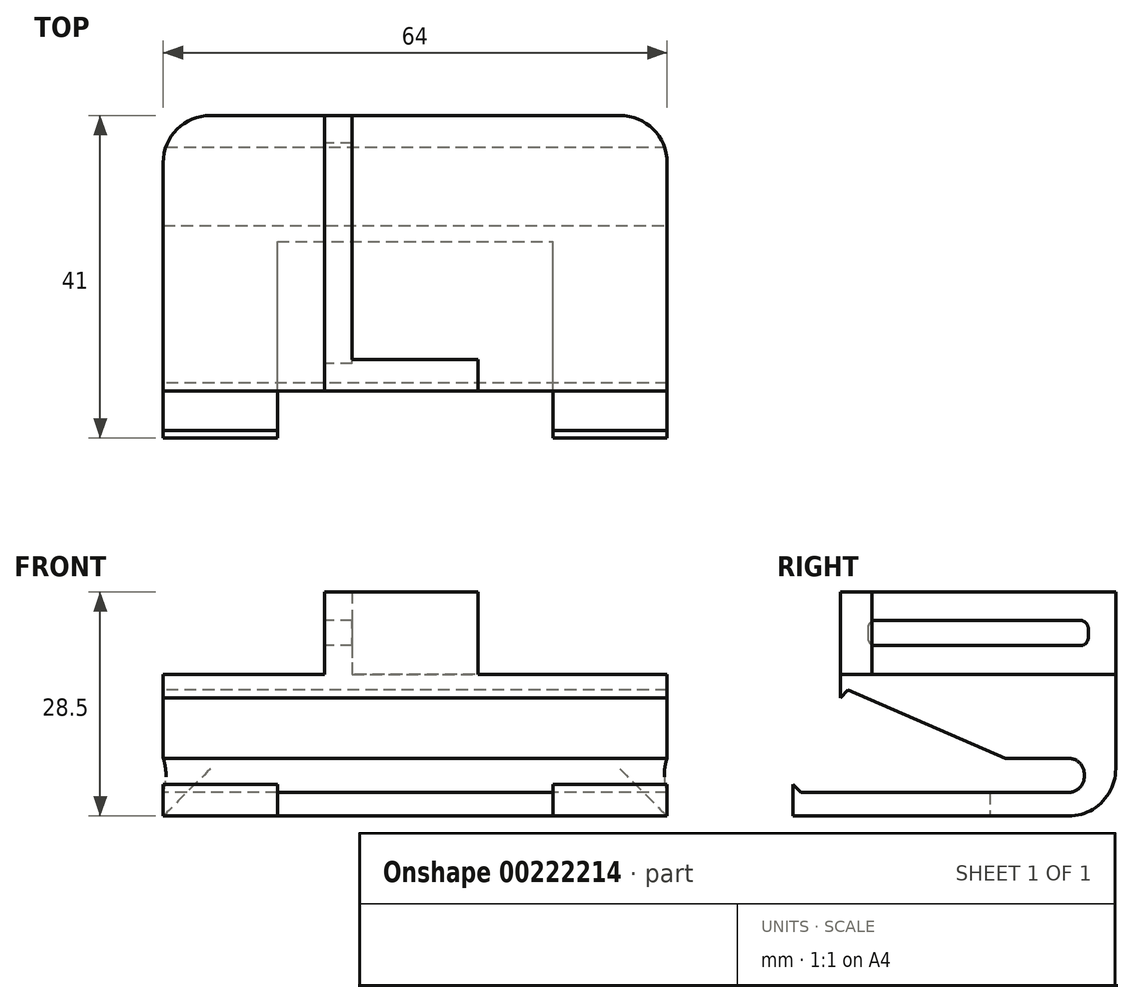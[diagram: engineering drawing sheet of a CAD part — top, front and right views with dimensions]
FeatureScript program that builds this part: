
annotation { "Feature Type Name" : "Feature", "Feature Type Description" : "" }
export const myFeature = defineFeature(function(context is Context, id is Id, definition is map)
    precondition{}
    {
        {
            var Q0;
            Q0=qCreatedBy(makeId("Right.planeOp"),FACE);
            var sketch = newSketch(context, id + "F0", { "sketchPlane" : qUnion([Q0])});
            skLineSegment(sketch, "E0", {"start": v(-22.5, -6) * mm, "end": v(13.5, -6) * mm});
            skLineSegment(sketch, "E1", {"start": v(13.5, -6) * mm, "end": v(-16.5, 7) * mm});
            skLineSegment(sketch, "E2", {"start": v(-16.5, 7) * mm, "end": v(-17.5, 6) * mm});
            skLineSegment(sketch, "E3", {"start": v(-17.5, 6) * mm, "end": v(-17.5, 9) * mm});
            skLineSegment(sketch, "E4", {"start": v(-17.5, 9) * mm, "end": v(17.5, 9) * mm});
            skLineSegment(sketch, "E5", {"start": v(17.5, 9) * mm, "end": v(17.5, -9) * mm});
            skLineSegment(sketch, "E6", {"start": v(17.5, -9) * mm, "end": v(-23.5, -9) * mm});
            skLineSegment(sketch, "E7", {"start": v(-23.5, -9) * mm, "end": v(-23.5, -5) * mm});
            skLineSegment(sketch, "E8", {"start": v(-23.5, -5) * mm, "end": v(-22.5, -6) * mm});
            skPoint(sketch, "E9", {"position": v(0, 9) * mm});
            skPoint(sketch, "E10", {"position": v(17.5, 0) * mm});
            skSolve(sketch);
        }
        {
            var Q0;
            Q0=makeQuery(id+"F0.imprint","IMPRINT",FACE,{"disambiguationData":[TD([[makeQuery(id+"F0.imprint","IMPRINT",EDGE,{"derivedFrom":sQuery(id+"F0.wireOp",EDGE,"E0")}),-1.0]])]});
            extrude(context, id + "F1", {"entities" : qUnion([Q0]), "endBound" : BoundingType.SYMMETRIC, "depth" : 64 * mm});
        }
        {
            var Q0;
            Q0=makeQuery(id+"F1.opExtrude","CAP_FACE",FACE,{"disambiguationData":[OSD([sQuery(id+"F0.wireOp",EDGE,"E0"),sQuery(id+"F0.wireOp",EDGE,"E1"),sQuery(id+"F0.wireOp",EDGE,"E2"),sQuery(id+"F0.wireOp",EDGE,"E3"),sQuery(id+"F0.wireOp",EDGE,"E4"),sQuery(id+"F0.wireOp",EDGE,"E5"),sQuery(id+"F0.wireOp",EDGE,"E6"),sQuery(id+"F0.wireOp",EDGE,"E7"),sQuery(id+"F0.wireOp",EDGE,"E8")])],"isStart":false});
            var sketch = newSketch(context, id + "F2", { "sketchPlane" : qUnion([Q0])});
            skLineSegment(sketch, "E11.bottom", {"start": v(13.5, -6) * mm, "end": v(3.5, -6) * mm});
            skLineSegment(sketch, "E11.top", {"start": v(11.5, -1.67) * mm, "end": v(3.5, -1.67) * mm});
            skLineSegment(sketch, "E11.left", {"start": v(13.5, -6) * mm, "end": v(13.5, -3.67) * mm});
            skLineSegment(sketch, "E11.right", {"start": v(3.5, -6) * mm, "end": v(3.5, -1.67) * mm});
            skPoint(sketch, "E12.visualSharp", {"position": v(13.5, -1.67) * mm});
            skArc(sketch, "E12.filletArc", {"start": v(13.5, -3.67) * mm, "mid": v(12.91, -2.25) * mm, "end": v(11.5, -1.67) * mm});
            skSolve(sketch);
        }
        {
            var Q0;
            {var subQ0=sQuery(id+"F2.wireOp",EDGE,"E11.top");Q0=makeQuery(id+"F2.imprint","IMPRINT",FACE,{"disambiguationData":[TD([[makeQuery(id+"F2.imprint","IMPRINT",EDGE,{"derivedFrom":subQ0}),1.0]])]});}
            extrude(context, id + "F3", {"entities" : qUnion([Q0]), "operationType" : NewBodyOperationType.REMOVE, "endBound" : BoundingType.UP_TO_NEXT, "oppositeDirection" : true, "depth" : 25 * mm});
        }
        {
            var Q0;
            Q0=makeQuery(id+"F1.opExtrude","SWEPT_FACE",FACE,{"disambiguationData":[OSD([sQuery(id+"F0.wireOp",EDGE,"E4")])]});
            var sketch = newSketch(context, id + "F4", { "sketchPlane" : qUnion([Q0])});
            skLineSegment(sketch, "E13.bottom", {"start": v(-11.5, 17.5) * mm, "end": v(-8, 17.5) * mm});
            skLineSegment(sketch, "E13.top", {"start": v(-11.5, -17.5) * mm, "end": v(-8, -17.5) * mm});
            skLineSegment(sketch, "E13.left", {"start": v(-11.5, 17.5) * mm, "end": v(-11.5, -17.5) * mm});
            skLineSegment(sketch, "E13.right", {"start": v(-8, 17.5) * mm, "end": v(-8, -17.5) * mm});
            skSolve(sketch);
        }
        {
            var Q0;
            Q0=makeQuery(id+"F4.imprint","IMPRINT",FACE,{"disambiguationData":[TD([[makeQuery(id+"F4.imprint","IMPRINT",EDGE,{"derivedFrom":sQuery(id+"F4.wireOp",EDGE,"E13.bottom")}),1.0]])]});
            extrude(context, id + "F5", {"entities" : qUnion([Q0]), "operationType" : NewBodyOperationType.ADD, "depth" : 10.5 * mm});
        }
        {
            var Q0;
            Q0=makeQuery(id+"F5.opExtrude","SWEPT_FACE",FACE,{"disambiguationData":[OSD([sQuery(id+"F4.wireOp",EDGE,"E13.left")])]});
            var sketch = newSketch(context, id + "F6", { "sketchPlane" : qUnion([Q0])});
            skLineSegment(sketch, "E14.bottom", {"start": v(-13, 15.85) * mm, "end": v(13, 15.85) * mm});
            skLineSegment(sketch, "E14.top", {"start": v(-13, 12.65) * mm, "end": v(13, 12.65) * mm});
            skLineSegment(sketch, "E14.left", {"start": v(-14, 14.85) * mm, "end": v(-14, 13.65) * mm});
            skLineSegment(sketch, "E14.right", {"start": v(14, 14.85) * mm, "end": v(14, 13.65) * mm});
            skPoint(sketch, "E15", {"position": v(-14, 14.25) * mm});
            skPoint(sketch, "E16", {"position": v(0, 15.85) * mm});
            skPoint(sketch, "E17", {"position": v(-17.5, 14.25) * mm});
            skPoint(sketch, "E18", {"position": v(0, 19.5) * mm});
            skPoint(sketch, "E19.visualSharp", {"position": v(-14, 15.85) * mm});
            skArc(sketch, "E19.filletArc", {"start": v(-13, 15.85) * mm, "mid": v(-13.7, 15.56) * mm, "end": v(-14, 14.85) * mm});
            skPoint(sketch, "E20.visualSharp", {"position": v(-14, 12.65) * mm});
            skArc(sketch, "E20.filletArc", {"start": v(-14, 13.65) * mm, "mid": v(-13.7, 12.94) * mm, "end": v(-13, 12.65) * mm});
            skPoint(sketch, "E21.visualSharp", {"position": v(14, 12.65) * mm});
            skArc(sketch, "E21.filletArc", {"start": v(13, 12.65) * mm, "mid": v(13.7, 12.94) * mm, "end": v(14, 13.65) * mm});
            skPoint(sketch, "E22.visualSharp", {"position": v(14, 15.85) * mm});
            skArc(sketch, "E22.filletArc", {"start": v(14, 14.85) * mm, "mid": v(13.7, 15.56) * mm, "end": v(13, 15.85) * mm});
            skSolve(sketch);
        }
        {
            var Q0;
            Q0=makeQuery(id+"F6.imprint","IMPRINT",FACE,{"disambiguationData":[TD([[makeQuery(id+"F6.imprint","IMPRINT",EDGE,{"derivedFrom":sQuery(id+"F6.wireOp",EDGE,"E14.bottom")}),-1.0]])]});
            extrude(context, id + "F7", {"entities" : qUnion([Q0]), "operationType" : NewBodyOperationType.REMOVE, "endBound" : BoundingType.UP_TO_NEXT, "oppositeDirection" : true, "depth" : 25 * mm});
        }
        {
            var Q0;
            {var subQ8=sQuery(id+"F4.wireOp",EDGE,"E13.right");var subQ9=makeQuery(id+"F5.opExtrude","SWEPT_FACE",FACE,{"disambiguationData":[OSD([subQ8])]});var subQ10=sQuery(id+"F0.wireOp",EDGE,"E4");Q0=makeQuery(id+"FXntyeOyRUhSL1L_1.1.F5.boolean.opBoolean","SPLIT",FACE,{"disambiguationData":[TD([subQ9])],"derivedFrom":makeQuery(id+"F5.boolean.opBoolean","SPLIT",FACE,{"disambiguationData":[TD([subQ9])],"derivedFrom":makeQuery(id+"F1.opExtrude","SWEPT_FACE",FACE,{"disambiguationData":[OSD([subQ10])]})})});}
            var sketch = newSketch(context, id + "F8", { "sketchPlane" : qUnion([Q0])});
            skLineSegment(sketch, "E23.bottom", {"start": v(-8, -17.5) * mm, "end": v(8, -17.5) * mm});
            skLineSegment(sketch, "E23.top", {"start": v(-8, -13.5) * mm, "end": v(8, -13.5) * mm});
            skLineSegment(sketch, "E23.left", {"start": v(-8, -17.5) * mm, "end": v(-8, -13.5) * mm});
            skLineSegment(sketch, "E23.right", {"start": v(8, -17.5) * mm, "end": v(8, -13.5) * mm});
            skSolve(sketch);
        }
        {
            var Q0;
            Q0=makeQuery(id+"F8.imprint","IMPRINT",FACE,{"disambiguationData":[TD([[makeQuery(id+"F8.imprint","IMPRINT",EDGE,{"derivedFrom":sQuery(id+"F8.wireOp",EDGE,"E23.bottom")}),-1.0]])]});
            var Q1;
            Q1=makeQuery(id+"F5.opExtrude","CAP_FACE",FACE,{"disambiguationData":[OSD([sQuery(id+"F4.wireOp",EDGE,"E13.bottom"),sQuery(id+"F4.wireOp",EDGE,"E13.top"),sQuery(id+"F4.wireOp",EDGE,"E13.left"),sQuery(id+"F4.wireOp",EDGE,"E13.right")])],"isStart":false});
            extrude(context, id + "F9", {"entities" : qUnion([Q0]), "operationType" : NewBodyOperationType.ADD, "endBound" : BoundingType.UP_TO_SURFACE, "endBoundEntityFace" : qUnion([Q1]), "depth" : 25 * mm});
        }
        {
            var Q0;
            Q0=makeQuery(id+"F1.opExtrude","CAP_EDGE",EDGE,{"disambiguationData":[OSD([sQuery(id+"F0.wireOp",EDGE,"E5")])],"isStart":false});
            var Q1;
            Q1=makeQuery(id+"F1.opExtrude","CAP_EDGE",EDGE,{"disambiguationData":[OSD([sQuery(id+"F0.wireOp",EDGE,"E5")])],"isStart":true});
            var Q2;
            Q2=makeQuery(id+"F1.opExtrude","SWEPT_EDGE",EDGE,{"disambiguationData":[OSD([sQuery(id+"F0.wireOp",EDGE,"E5"),sQuery(id+"F0.wireOp",EDGE,"E6")])]});
            fillet(context, id + "F10", {"entities" : qUnion([Q0, Q1, Q2]), "radius" : 6 * mm, "tangentPropagation" : true, "allowEdgeOverflow" : false});
        }
        {
            var Q0;
            Q0=makeQuery(id+"F1.opExtrude","SWEPT_FACE",FACE,{"disambiguationData":[OSD([sQuery(id+"F0.wireOp",EDGE,"E6")])]});
            var sketch = newSketch(context, id + "F11", { "sketchPlane" : qUnion([Q0])});
            skLineSegment(sketch, "E24.bottom", {"start": v(-17.5, 23.5) * mm, "end": v(17.5, 23.5) * mm});
            skLineSegment(sketch, "E24.top", {"start": v(-17.5, -1.5) * mm, "end": v(17.5, -1.5) * mm});
            skLineSegment(sketch, "E24.left", {"start": v(-17.5, 23.5) * mm, "end": v(-17.5, -1.5) * mm});
            skLineSegment(sketch, "E24.right", {"start": v(17.5, 23.5) * mm, "end": v(17.5, -1.5) * mm});
            skPoint(sketch, "E25", {"position": v(0, 23.5) * mm});
            skSolve(sketch);
        }
        {
            var Q0;
            Q0=makeQuery(id+"F11.imprint","IMPRINT",FACE,{"disambiguationData":[TD([[makeQuery(id+"F11.imprint","IMPRINT",EDGE,{"derivedFrom":sQuery(id+"F11.wireOp",EDGE,"E24.bottom")}),1.0]])]});
            extrude(context, id + "F12", {"entities" : qUnion([Q0]), "operationType" : NewBodyOperationType.REMOVE, "endBound" : BoundingType.UP_TO_NEXT, "oppositeDirection" : true, "depth" : 25 * mm});
        }
        {
            var Q0;
            {var subQ0=sQuery(id+"F0.wireOp",EDGE,"E1");var subQ1=sQuery(id+"F0.wireOp",EDGE,"E0");Q0=makeQuery(id+"F3.boolean.opBoolean","MERGE",EDGE,{"derivedFrom":[makeQuery(id+"F1.opExtrude","SWEPT_EDGE",EDGE,{"disambiguationData":[OSD([subQ1,subQ0])]}),makeQuery(id+"F3.opExtrude","SWEPT_EDGE",EDGE,{"disambiguationData":[OSD([subQ1,subQ0,sQuery(id+"F2.wireOp",EDGE,"E11.bottom"),sQuery(id+"F2.wireOp",EDGE,"E11.left")])]})]});}
            fillet(context, id + "F13", {"entities" : qUnion([Q0]), "radius" : 2 * mm, "tangentPropagation" : true, "allowEdgeOverflow" : false});
        }
    });
